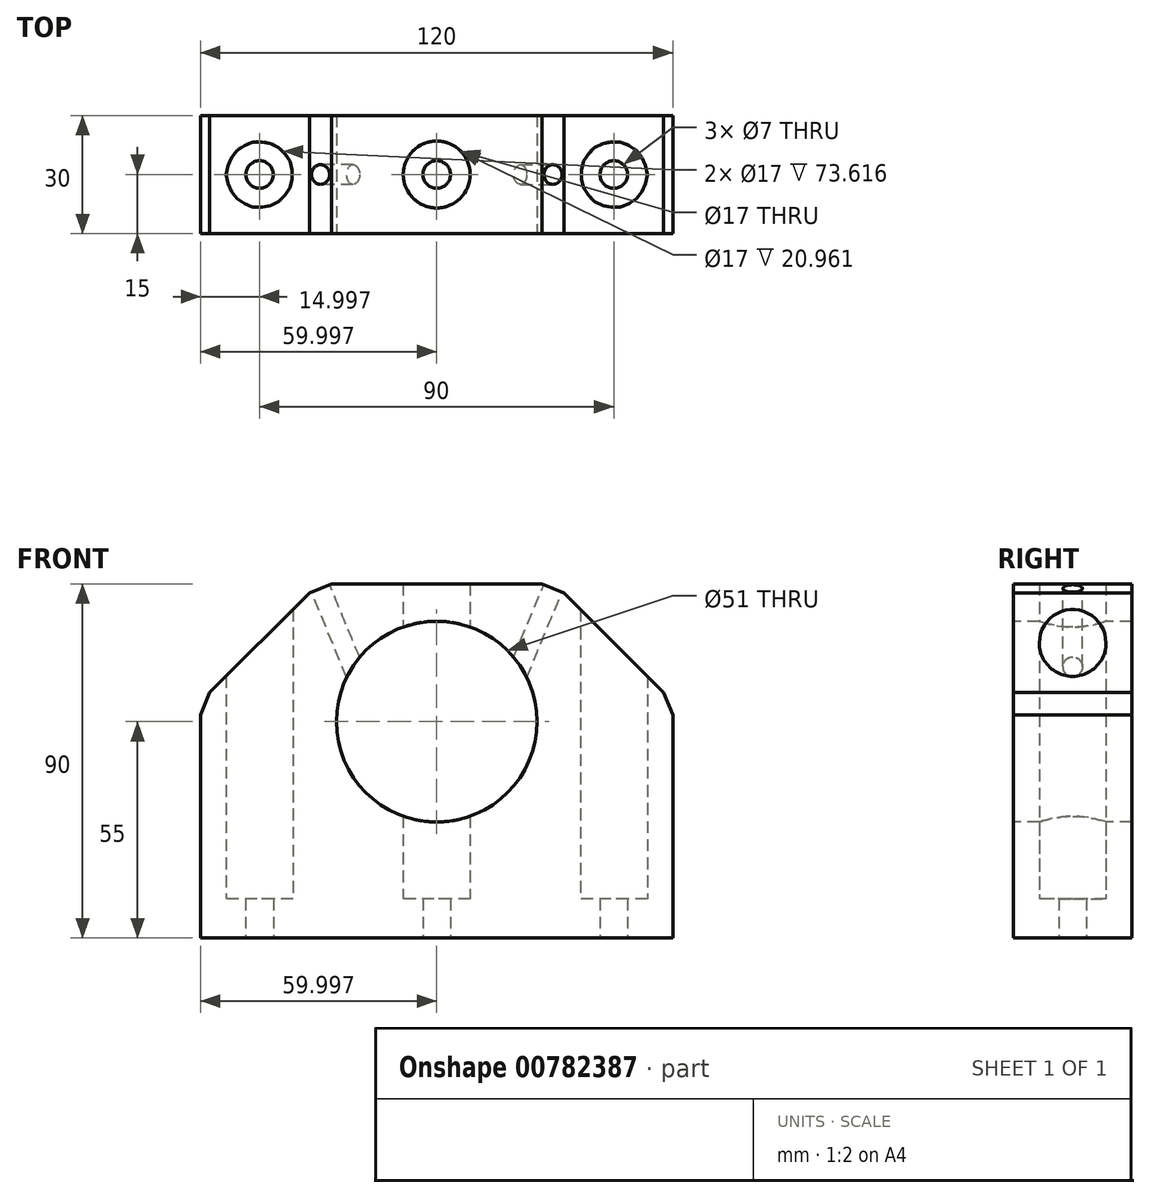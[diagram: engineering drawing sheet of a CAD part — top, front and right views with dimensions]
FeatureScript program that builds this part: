
annotation { "Feature Type Name" : "Feature", "Feature Type Description" : "" }
export const myFeature = defineFeature(function(context is Context, id is Id, definition is map)
    precondition{}
    {
        {
            var Q0;
            Q0=qCreatedBy(makeId("Top.planeOp"),FACE);
            var sketch = newSketch(context, id + "F0", { "sketchPlane" : qUnion([Q0])});
            skCircle(sketch, "E0", {"center": v(-50.43, 0) * mm, "radius": 3.5 * mm});
            skCircle(sketch, "E1", {"center": v(39.57, 0) * mm, "radius": 3.5 * mm});
            skCircle(sketch, "E2", {"center": v(-5.43, 0) * mm, "radius": 3.5 * mm});
            skLineSegment(sketch, "E3.bottom", {"start": v(-65.43, 15) * mm, "end": v(54.57, 15) * mm});
            skLineSegment(sketch, "E3.top", {"start": v(-65.43, -15) * mm, "end": v(54.57, -15) * mm});
            skLineSegment(sketch, "E3.left", {"start": v(-65.43, 15) * mm, "end": v(-65.43, -15) * mm});
            skLineSegment(sketch, "E3.right", {"start": v(54.57, 15) * mm, "end": v(54.57, -15) * mm});
            skSolve(sketch);
        }
        {
            var Q0;
            Q0=makeQuery(id+"F0.imprint","IMPRINT",FACE,{"disambiguationData":[TD([[makeQuery(id+"F0.imprint","IMPRINT",EDGE,{"derivedFrom":sQuery(id+"F0.wireOp",EDGE,"E0")}),-1.0]])]});
            extrude(context, id + "F1", {"entities" : qUnion([Q0]), "depth" : 10 * mm, "offsetDistance" : 25 * mm});
        }
        {
            var Q0;
            Q0=makeQuery(id+"F1.opExtrude","CAP_FACE",FACE,{"disambiguationData":[OSD([sQuery(id+"F0.wireOp",EDGE,"E0"),sQuery(id+"F0.wireOp",EDGE,"E1"),sQuery(id+"F0.wireOp",EDGE,"E2"),sQuery(id+"F0.wireOp",EDGE,"E3.bottom"),sQuery(id+"F0.wireOp",EDGE,"E3.top"),sQuery(id+"F0.wireOp",EDGE,"E3.left"),sQuery(id+"F0.wireOp",EDGE,"E3.right")])],"isStart":false});
            var sketch = newSketch(context, id + "F2", { "sketchPlane" : qUnion([Q0])});
            skCircle(sketch, "E4", {"center": v(-50.43, 0) * mm, "radius": 8.5 * mm});
            skCircle(sketch, "E5", {"center": v(-5.43, 0) * mm, "radius": 8.5 * mm});
            skCircle(sketch, "E6", {"center": v(39.57, 0) * mm, "radius": 8.5 * mm});
            skLineSegment(sketch, "E7.bottom", {"start": v(-65.43, 15) * mm, "end": v(54.57, 15) * mm});
            skLineSegment(sketch, "E7.top", {"start": v(-65.43, -15) * mm, "end": v(54.57, -15) * mm});
            skLineSegment(sketch, "E7.left", {"start": v(-65.43, 15) * mm, "end": v(-65.43, -15) * mm});
            skLineSegment(sketch, "E7.right", {"start": v(54.57, 15) * mm, "end": v(54.57, -15) * mm});
            skLineSegment(sketch, "E8.bottom", {"start": v(-74.43, 22) * mm, "end": v(63.57, 22) * mm});
            skLineSegment(sketch, "E8.top", {"start": v(-74.43, -38) * mm, "end": v(63.57, -38) * mm});
            skLineSegment(sketch, "E8.left", {"start": v(-74.43, 22) * mm, "end": v(-74.43, -38) * mm});
            skLineSegment(sketch, "E8.right", {"start": v(63.57, 22) * mm, "end": v(63.57, -38) * mm});
            skSolve(sketch);
        }
        {
            var Q0;
            Q0=makeQuery(id+"F2.imprint","IMPRINT",FACE,{"disambiguationData":[TD([[makeQuery(id+"F2.imprint","IMPRINT",EDGE,{"derivedFrom":sQuery(id+"F2.wireOp",EDGE,"E4")}),-1.0]])]});
            extrude(context, id + "F3", {"entities" : qUnion([Q0]), "operationType" : NewBodyOperationType.ADD, "depth" : 80 * mm, "offsetDistance" : 25 * mm});
        }
        {
            var Q0;
            {var subQ0=sQuery(id+"F2.wireOp",EDGE,"E7.left");var subQ1=sQuery(id+"F2.wireOp",EDGE,"E7.right");var subQ2=sQuery(id+"F2.wireOp",EDGE,"E7.top");var subQ3=sQuery(id+"F2.wireOp",EDGE,"E7.bottom");Q0=makeQuery(id+"F6neVGVIBLqQV2m_1.boolean.opBoolean","SPLIT",FACE,{"disambiguationData":[TD([makeQuery(id+"F3.opExtrude","CAP_FACE",FACE,{"disambiguationData":[OSD([sQuery(id+"F2.wireOp",EDGE,"E4"),sQuery(id+"F2.wireOp",EDGE,"E5"),sQuery(id+"F2.wireOp",EDGE,"E6"),subQ3,subQ2,subQ0,subQ1])],"isStart":false})])],"derivedFrom":makeQuery(id+"F3.boolean.opBoolean","MERGE",FACE,{"derivedFrom":[makeQuery(id+"F1.opExtrude","SWEPT_FACE",FACE,{"disambiguationData":[OSD([sQuery(id+"F0.wireOp",EDGE,"E3.top")])]}),makeQuery(id+"F3.opExtrude","SWEPT_FACE",FACE,{"disambiguationData":[OSD([subQ2])]})]})});}
            var sketch = newSketch(context, id + "F4", { "sketchPlane" : qUnion([Q0])});
            skCircle(sketch, "E9", {"center": v(-5.43, 55) * mm, "radius": 25.5 * mm});
            skSolve(sketch);
        }
        {
            var Q0;
            Q0 = qSketchRegion(id + "F4", true);
            extrude(context, id + "F5", {"entities" : qUnion([Q0]), "operationType" : NewBodyOperationType.REMOVE, "oppositeDirection" : true, "depth" : 30 * mm, "offsetDistance" : 25 * mm});
        }
        {
            var Q0;
            Q0=makeQuery(id+"F3.opExtrude","CAP_EDGE",EDGE,{"disambiguationData":[OSD([sQuery(id+"F2.wireOp",EDGE,"E7.left")])],"isStart":false});
            var Q1;
            Q1=makeQuery(id+"F3.opExtrude","CAP_EDGE",EDGE,{"disambiguationData":[OSD([sQuery(id+"F2.wireOp",EDGE,"E7.right")])],"isStart":false});
            chamfer(context, id + "F6", {"entities" : qUnion([Q0, Q1]), "width" : 30 * mm, "tangentPropagation" : true});
        }
        {
            var Q0;
            {var subQ0=sQuery(id+"F2.wireOp",EDGE,"E7.left");Q0=makeQuery(id+"F6.opChamfer","BLEND_EDGE",EDGE,{"blendedFrom":[makeQuery(id+"F3.opExtrude","CAP_EDGE",EDGE,{"disambiguationData":[OSD([subQ0])],"isStart":false}),makeQuery(id+"F3.boolean.opBoolean","MERGE",FACE,{"derivedFrom":[makeQuery(id+"F1.opExtrude","SWEPT_FACE",FACE,{"disambiguationData":[OSD([sQuery(id+"F0.wireOp",EDGE,"E3.left")])]}),makeQuery(id+"F3.opExtrude","SWEPT_FACE",FACE,{"disambiguationData":[OSD([subQ0])]})]})],"blendedInto":[makeQuery(id+"F3.boolean.opBoolean","MERGE",FACE,{"derivedFrom":[makeQuery(id+"F1.opExtrude","SWEPT_FACE",FACE,{"disambiguationData":[OSD([sQuery(id+"F0.wireOp",EDGE,"E3.left")])]}),makeQuery(id+"F3.opExtrude","SWEPT_FACE",FACE,{"disambiguationData":[OSD([subQ0])]})]})]});}
            var Q1;
            {var subQ0=sQuery(id+"F2.wireOp",EDGE,"E7.left");Q1=makeQuery(id+"F6.opChamfer","BLEND_EDGE",EDGE,{"blendedFrom":[makeQuery(id+"F3.opExtrude","CAP_EDGE",EDGE,{"disambiguationData":[OSD([subQ0])],"isStart":false}),makeQuery(id+"F3.opExtrude","CAP_FACE",FACE,{"disambiguationData":[OSD([sQuery(id+"F2.wireOp",EDGE,"E4"),sQuery(id+"F2.wireOp",EDGE,"E5"),sQuery(id+"F2.wireOp",EDGE,"E6"),sQuery(id+"F2.wireOp",EDGE,"E7.bottom"),sQuery(id+"F2.wireOp",EDGE,"E7.top"),subQ0,sQuery(id+"F2.wireOp",EDGE,"E7.right")])],"isStart":false})],"blendedInto":[makeQuery(id+"F3.opExtrude","CAP_FACE",FACE,{"disambiguationData":[OSD([sQuery(id+"F2.wireOp",EDGE,"E4"),sQuery(id+"F2.wireOp",EDGE,"E5"),sQuery(id+"F2.wireOp",EDGE,"E6"),sQuery(id+"F2.wireOp",EDGE,"E7.bottom"),sQuery(id+"F2.wireOp",EDGE,"E7.top"),subQ0,sQuery(id+"F2.wireOp",EDGE,"E7.right")])],"isStart":false})]});}
            var Q2;
            {var subQ0=sQuery(id+"F2.wireOp",EDGE,"E7.right");Q2=makeQuery(id+"F6.opChamfer","BLEND_EDGE",EDGE,{"blendedFrom":[makeQuery(id+"F3.opExtrude","CAP_EDGE",EDGE,{"disambiguationData":[OSD([subQ0])],"isStart":false}),makeQuery(id+"F3.opExtrude","CAP_FACE",FACE,{"disambiguationData":[OSD([sQuery(id+"F2.wireOp",EDGE,"E4"),sQuery(id+"F2.wireOp",EDGE,"E5"),sQuery(id+"F2.wireOp",EDGE,"E6"),sQuery(id+"F2.wireOp",EDGE,"E7.bottom"),sQuery(id+"F2.wireOp",EDGE,"E7.top"),sQuery(id+"F2.wireOp",EDGE,"E7.left"),subQ0])],"isStart":false})],"blendedInto":[makeQuery(id+"F3.opExtrude","CAP_FACE",FACE,{"disambiguationData":[OSD([sQuery(id+"F2.wireOp",EDGE,"E4"),sQuery(id+"F2.wireOp",EDGE,"E5"),sQuery(id+"F2.wireOp",EDGE,"E6"),sQuery(id+"F2.wireOp",EDGE,"E7.bottom"),sQuery(id+"F2.wireOp",EDGE,"E7.top"),sQuery(id+"F2.wireOp",EDGE,"E7.left"),subQ0])],"isStart":false})]});}
            var Q3;
            {var subQ0=sQuery(id+"F2.wireOp",EDGE,"E7.right");Q3=makeQuery(id+"F6.opChamfer","BLEND_EDGE",EDGE,{"blendedFrom":[makeQuery(id+"F3.opExtrude","CAP_EDGE",EDGE,{"disambiguationData":[OSD([subQ0])],"isStart":false}),makeQuery(id+"F3.boolean.opBoolean","MERGE",FACE,{"derivedFrom":[makeQuery(id+"F1.opExtrude","SWEPT_FACE",FACE,{"disambiguationData":[OSD([sQuery(id+"F0.wireOp",EDGE,"E3.right")])]}),makeQuery(id+"F3.opExtrude","SWEPT_FACE",FACE,{"disambiguationData":[OSD([subQ0])]})]})],"blendedInto":[makeQuery(id+"F3.boolean.opBoolean","MERGE",FACE,{"derivedFrom":[makeQuery(id+"F1.opExtrude","SWEPT_FACE",FACE,{"disambiguationData":[OSD([sQuery(id+"F0.wireOp",EDGE,"E3.right")])]}),makeQuery(id+"F3.opExtrude","SWEPT_FACE",FACE,{"disambiguationData":[OSD([subQ0])]})]})]});}
            chamfer(context, id + "F7", {"entities" : qUnion([Q0, Q1, Q2, Q3]), "width" : 8 * mm, "tangentPropagation" : true});
        }
        {
            var Q0;
            {var subQ0=sQuery(id+"F2.wireOp",EDGE,"E7.right");var subQ1=sQuery(id+"F2.wireOp",EDGE,"E7.left");var subQ2=sQuery(id+"F2.wireOp",EDGE,"E7.top");var subQ3=sQuery(id+"F2.wireOp",EDGE,"E7.bottom");var subQ4=sQuery(id+"F2.wireOp",EDGE,"E6");var subQ5=sQuery(id+"F2.wireOp",EDGE,"E5");var subQ6=sQuery(id+"F2.wireOp",EDGE,"E4");Q0=makeQuery(id+"F7.opChamfer","BLEND_FACE",FACE,{"disambiguationData":[OSD([subQ6,subQ5,subQ4,subQ3,subQ2,subQ1,subQ0]),TDD([makeQuery(id+"F6.opChamfer","BLEND_EDGE",EDGE,{"blendedFrom":[makeQuery(id+"F3.opExtrude","CAP_EDGE",EDGE,{"disambiguationData":[OSD([subQ1])],"isStart":false}),makeQuery(id+"F3.opExtrude","CAP_FACE",FACE,{"disambiguationData":[OSD([subQ6,subQ5,subQ4,subQ3,subQ2,subQ1,subQ0])],"isStart":false})],"blendedInto":[makeQuery(id+"F3.opExtrude","CAP_FACE",FACE,{"disambiguationData":[OSD([subQ6,subQ5,subQ4,subQ3,subQ2,subQ1,subQ0])],"isStart":false})]})])]});}
            var sketch = newSketch(context, id + "F8", { "sketchPlane" : qUnion([Q0])});
            skLineSegment(sketch, "E10", {"start": v(-5.69, 15) * mm, "end": v(9.1, -15) * mm});
            skLineSegment(sketch, "E11", {"start": v(9.1, -15) * mm, "end": v(-5.69, -15) * mm});
            skLineSegment(sketch, "E12", {"start": v(-5.69, -15) * mm, "end": v(9.1, 15) * mm});
            skPoint(sketch, "E13", {"position": v(1.7, 0) * mm});
            skSolve(sketch);
        }
        {
            var Q0;
            {var subQ0=sQuery(id+"F2.wireOp",EDGE,"E7.right");var subQ1=sQuery(id+"F2.wireOp",EDGE,"E7.left");var subQ2=sQuery(id+"F2.wireOp",EDGE,"E7.top");var subQ3=sQuery(id+"F2.wireOp",EDGE,"E7.bottom");var subQ4=sQuery(id+"F2.wireOp",EDGE,"E6");var subQ5=sQuery(id+"F2.wireOp",EDGE,"E5");var subQ6=sQuery(id+"F2.wireOp",EDGE,"E4");Q0=makeQuery(id+"F7.opChamfer","BLEND_FACE",FACE,{"disambiguationData":[OSD([subQ6,subQ5,subQ4,subQ3,subQ2,subQ1,subQ0]),TDD([makeQuery(id+"F6.opChamfer","BLEND_EDGE",EDGE,{"blendedFrom":[makeQuery(id+"F3.opExtrude","CAP_EDGE",EDGE,{"disambiguationData":[OSD([subQ0])],"isStart":false}),makeQuery(id+"F3.opExtrude","CAP_FACE",FACE,{"disambiguationData":[OSD([subQ6,subQ5,subQ4,subQ3,subQ2,subQ1,subQ0])],"isStart":false})],"blendedInto":[makeQuery(id+"F3.opExtrude","CAP_FACE",FACE,{"disambiguationData":[OSD([subQ6,subQ5,subQ4,subQ3,subQ2,subQ1,subQ0])],"isStart":false})]})])]});}
            var sketch = newSketch(context, id + "F9", { "sketchPlane" : qUnion([Q0])});
            skLineSegment(sketch, "E14", {"start": v(-4.35, -15) * mm, "end": v(-19.14, 15) * mm});
            skLineSegment(sketch, "E15", {"start": v(-19.14, 15) * mm, "end": v(-19.14, -15) * mm});
            skLineSegment(sketch, "E16", {"start": v(-19.14, -15) * mm, "end": v(-4.35, 15) * mm});
            skPoint(sketch, "E17", {"position": v(-11.74, 0) * mm});
            skSolve(sketch);
        }
        {
            var Q0;
            Q0=sQuery(id+"F8.wireOp",VERTEX,"E13");
            var Q1;
            Q1=sQuery(id+"F9.wireOp",VERTEX,"E17");
            var Q2;
            Q2=makeQuery(id+"F1.opExtrude","SWEPT_BODY",BODY,{"disambiguationData":[OSD([sQuery(id+"F0.wireOp",EDGE,"E0"),sQuery(id+"F0.wireOp",EDGE,"E1"),sQuery(id+"F0.wireOp",EDGE,"E2"),sQuery(id+"F0.wireOp",EDGE,"E3.bottom"),sQuery(id+"F0.wireOp",EDGE,"E3.top"),sQuery(id+"F0.wireOp",EDGE,"E3.left"),sQuery(id+"F0.wireOp",EDGE,"E3.right")])]});
            hole(context, id + "F10", {"style" : HoleStyle.SIMPLE, "endStyle" : HoleEndStyle.BLIND, "holeDiameter" : 5 * mm, "majorDiameter" : 5 * mm, "holeDepth" : 25 * mm, "isTappedThrough" : true, "tappedDepth" : 12 * mm, "tapClearance" : 3, "startFromSketch" : true, "locations" : qUnion([Q0, Q1]), "scope" : qUnion([Q2])});
        }
    });
